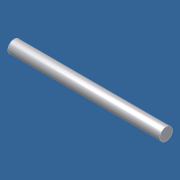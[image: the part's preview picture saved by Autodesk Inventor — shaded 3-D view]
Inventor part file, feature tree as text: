
AUTODESK INVENTOR PART (.ipt)
format: ipt  version: unknown  size: 159,744 bytes
history: native  units: in
note: dims shown in document units (in); Inventor stores cm internally (conversion verified against a paired STEP export)
features: revolve x1, sketch x1
ambient origin geometry x8: Origin, YZ Plane, XZ Plane, XY Plane, X Axis, Y Axis, Z Axis, Center Point
bodies: Solid1 (feature_tree)
feature tree (2):
  revolve  "Revolution1"  [1 undecoded]
  sketch  "Sketch1"  dims[d0=0.125in d1=3.0in d2=90.0deg]
note: 1 required parameter value undecoded (feature->parameter linkage not recoverable at this tier; creation-order binding heuristic only, values carry confidence <= 0.55)
